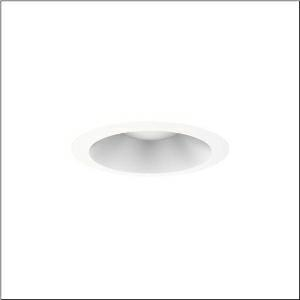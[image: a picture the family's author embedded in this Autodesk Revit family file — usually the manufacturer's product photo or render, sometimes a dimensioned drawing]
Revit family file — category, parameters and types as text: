
# Revit family: lunis_31-xl_51dn15eg42b
name_source: partatom
category: Lighting Fixtures
units: mm (PartAtom-declared; Revit-internal decimal feet)

## family parameters
Cut with Voids When Loaded = No
Host = Face
Light Source = No
Part Type = Normal
Room Calculation Point = No
Round Connector Dimension = Use Diameter
Shared = No

## types (1)
- --- (1 x LED, 2500 lm, 17.5 W, 4000K)
    Apparent Load = 18 VA
    CIE Flux Codes = 89 99 100 100 100
    Color Rendering = 80
    Color Temperature = 4000K
    Default Elevation = 1800 mm
    Description = Lunis 31, -XL, downlight, light control with lens, light emission: direct distribution, LED rated luminous flux: 2.500lm, light colour: 840, mains connection: 220..240V, AC, 50/60Hz, housing, of aluminium, white, protection rating (complete): IP20, protection rating (on room side): IP54, insulation class (complete): insulation class II (safety insulation), certification: CE, packaging unit: 1 piece
    Height = 0 mm  [stored 0 ft]
    Lamp = 1 x LED
    Lamp Light Flux = 2500 lm
    Lamp Power = 17.5 W
    Lamp count = 1
    Length = 259 mm
    Luminous efficacy = 143 lm/W
    Manufacturer = Siteco
    ModVariant = No
    Model = 51DN15EG42B
    Mounting Place = Ceiling
    Mounting Type = Recessed
    Number of Poles = 1
    OnlyDefault = Yes
    Power Factor = 1
    Product Name = Lunis 31-XL
    Product group = downlight
    ProductGroupID = 400
    Protection Class = Protection class II
    Protection Degree = IP 20
    RLX_Detail_Level = 1
    RLX_Emergency_Light_Flux = 0 lm
    RLX_Emergency_Type = 0
    RLX_Emergency_Type_DB = No
    RlxData = <blob elided: 24257 chars, md5=4eeb8c44>
    Socket = socket
    Standby Power = 0 W
    System Light Flux = 2500 lm
    System Power = 18 W
    Type Comments = individual setting: luminous flux: 100 % | (ON | OFF | ON) | 450 mA
    Type Image = l_1345915.jpg
    URL = http://relux.com
    VarID = @adj_010069
    Voltage = 0 V
    Weight = 0.00 kg
    Width = 0 mm  [stored 0 ft]

note: [stored X ft] marks values corroborated as IEEE doubles in the binary element streams (Revit-internal decimal feet)

## geometry (parser evidence)
native form markers: Blend x4, Sweep x10
no freeform markers — native parametric forms only
